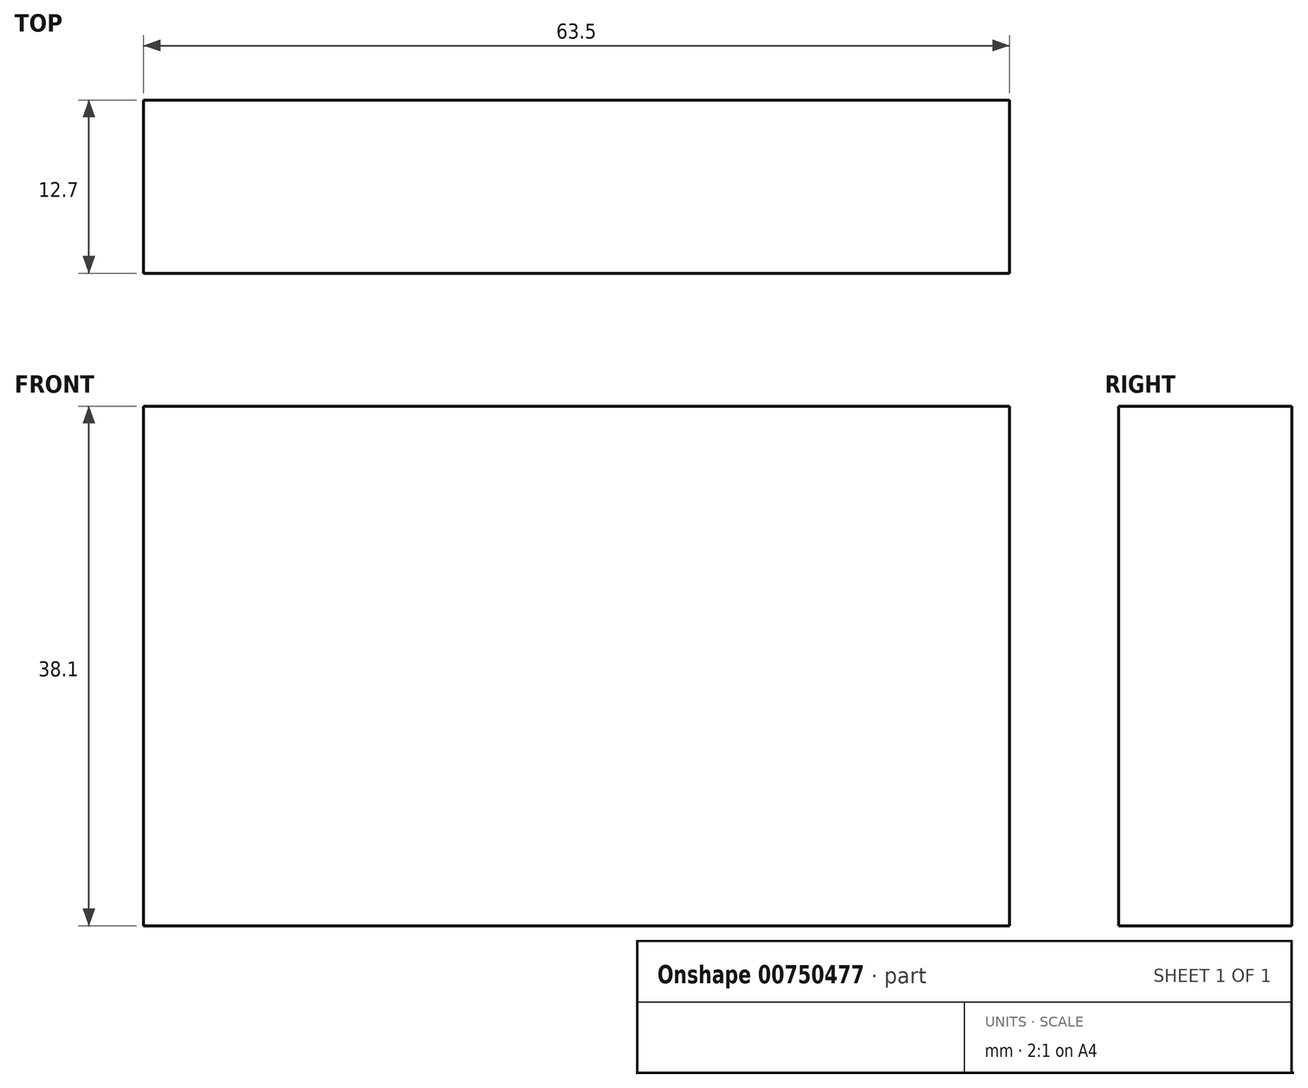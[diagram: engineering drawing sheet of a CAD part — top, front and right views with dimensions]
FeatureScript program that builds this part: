
annotation { "Feature Type Name" : "Feature", "Feature Type Description" : "" }
export const myFeature = defineFeature(function(context is Context, id is Id, definition is map)
    precondition{}
    {
        {
            var Q0;
            Q0=qCreatedBy(makeId("Front.planeOp"),FACE);
            var sketch = newSketch(context, id + "F0", { "sketchPlane" : qUnion([Q0])});
            skLineSegment(sketch, "E0.bottom", {"start": v(31.75, 19.05) * mm, "end": v(-31.75, 19.05) * mm});
            skLineSegment(sketch, "E0.top", {"start": v(31.75, -19.05) * mm, "end": v(-31.75, -19.05) * mm});
            skLineSegment(sketch, "E0.left", {"start": v(31.75, 19.05) * mm, "end": v(31.75, -19.05) * mm});
            skLineSegment(sketch, "E0.right", {"start": v(-31.75, 19.05) * mm, "end": v(-31.75, -19.05) * mm});
            skPoint(sketch, "E0.middle", {"position": v(0, 0) * mm});
            skSolve(sketch);
        }
        {
            var Q0;
            Q0=makeQuery(id+"F0.imprint","IMPRINT",FACE,{"disambiguationData":[TD([[makeQuery(id+"F0.imprint","IMPRINT",EDGE,{"derivedFrom":sQuery(id+"F0.wireOp",EDGE,"E0.bottom")}),1.0]])]});
            extrude(context, id + "F1", {"entities" : qUnion([Q0]), "depth" : 12.7 * mm, "offsetDistance" : 25.4 * mm});
        }
    });
